# Revit family: IS_Linda-X_T4401_BIM_NL
name_source: partatom
category: Plumbing Fixtures
units: mm (PartAtom-declared; Revit-internal decimal feet)

## family parameters
Always vertical = No
Cut with Voids When Loaded = No
OmniClass Number = 23.45.05.14.14
OmniClass Title = Sinks/Lavatories
Part Type = Normal
Room Calculation Point = No
Round Connector Dimension = Use Diameter
Shared = No
Work Plane-Based = No

## types (13) — shared parameters
Accesoires = https://www.idealstandard.nl
Accessories = https://www.idealstandard.nl
Afmetingen = 380 x 153 x 550mm
AfstandsEenheid = Millimeter
AreaUnits = Millimeter
Artikelomschrijving = Linda-X Gefäßbecken 55cm, ohne Hahnlöcher, geschlitzter Überlauf
Artikelreferentie = Linda-X Vessel Basin 55cm, No Tap Holes, Slotted Overflow
Auteur = Idea Standard
BIMObjectName = IS_IdealStandard_Wallhungwashbasins_Linda-X_T4401
BIMobject category = Sanitary Basins
BIMobject category code = sanitary-basins
BIMobject main category = Sanitary
BIMobject main category code = sanitary
Beschrijvinggarantie = Herstellergarantie
BimObjectNaam = IS_IdealStandard_Wallhungwashbasins_Linda-X_T4401
Brand = Idea Standard
Brand url = http://www.idealstandard.nl
ConnectionType = Plumbing
CurrencyUnit = €
CurrentRevision = 1
Date of publishing = 14/07/2021
Description = Linda-X Gefäßbecken 55cm, ohne Hahnlöcher, geschlitzter Überlauf
DurationUnit = Years
DuurEenheid = Jahre
Edition number = 1
Eigenschappen = Gefäßbecken 55cm, ohne Hahnlöcher, geschlitzter Überlauf
ElementType = Fixed
Features = Gefäßbecken 55cm, ohne Hahnlöcher, geschlitzter Überlauf
Garantieunits = Jahren
Help = https://www.idealstandard.nl
Hoogte = 153.310487747192
Hulp = https://www.idealstandard.nl
IFC Classification = Sanitary Terminal
IfcExportAs = IfcSanitaryTerminalType
IfcExportType = WASHHANDBASIN
Installatieinstructies = https://www.idealstandard.nl
Installation instructions = https://www.idealstandard.nl
InstallationInstructions = https://www.idealstandard.nl
Lengte = 380 mm
LinearUnits = Millimetres
MaintenanceInformation = https://www.idealstandard.nl
Manufacturer = Ideal Standard
Manufacturer name = Ideal Standard
ManufacturerURL = https://www.idealstandard.nl
Masterformat 2014 Code = 33 44 13.13
Masterformat 2014 Description = Catchbasins
Materiaal = Keramik
Material = Diamatec
Material main = Keramik
Merk = Ideal Standard
ModelReference = Linda-X Vessel Basin 55cm, No Tap Holes, Slotted Overflow
Montageinstuctie = https://www.idealstandard.nl
NBS Reference Code = 45-35-70/369
NBS Reference Description = Wall hung wash basins
Name = Wallhungwashbasins_Linda-X_T4401_IdealStandard
NettWeight = 12.4
NominalDepth = 380 mm
NominalHeight = 153 mm
NominalWidth = 550 mm
Normen = Wallhungwashbasins_Linda-X_T4401_IdealStandard
OmniClass Code = 23-39 29 13 21 19
OmniClass Description = Surface Water Retention Basins
Ophangingwastafel = Wand oder Sockel installiert
OppervlakteEenheid = Millimeter
Product Guid = 11f8b192-65c3-4091-a7fc-1ee436633e5b
Product SKU = T4401
Product certification = https://www.idealstandard.nl
Product data url = https://bimobject.com
Product family = Linda-X
Product group = Washbasins
Product name = Linda-X Vessel Basin 55cm, No Tap Holes, Slotted Overflow
Product url = https://www.idealstandard.nl
ProductInformation = https://www.idealstandard.nl
Productinformatie = https://www.idealstandard.nl
QR code = http://bimobject.com
Referentie = Linda-X Vessel Basin 55cm, No Tap Holes, Slotted Overflow
Revisie = 1
Shape = Oval
Size = 380 x 153 x 550mm
Space = Internal
SpareParts = https://www.idealstandard.nl
Technical description = https://www.idealstandard.nl
Telefoonnummer = 077 355 08 08
Typeconnectie = Installation
Typewastafel = Oval, Wand oder Sockel installiert
UNSPSC Code = 301815
URL = https://www.idealstandard.nl
Uniclass 1.4 Code = L7212
Uniclass 1.4 Description = Washbasins
Uniclass 2.0 Code = PR-31-79
Uniclass 2.0 Description = Sinks, Wash Basins And Troughs
Uniclass 2015 Code = Pr_40_20_96_96
Uniclass 2015 Name = Wall-hung washbasins
Uniclass2015Beschrijving = Wall-hung washbasins
Uniclass2015Code = Pr_40_20_96_96
Uniclass2015Referentie = Pr_40_20_96_96
Uniclass2015Title = Wall-hung washbasins
Uniclass2015Version = v1.20
Urlproducent = https://www.idealstandard.nl
ValutaEenheid = €
Versie = 1
Version = 1
VolumeUnits = Litres
Volumeunits = Liter
Vorm = Oval
WRASURL = https://www.wrasapprovals.co.uk
WarrantyDescription = Manufacturer Warranty
WarrantyDurationUnit = 5
WashHandBasinMounting = Wall Hung
WashHandBasinType = Vessel Wash Basin
Wisselstukken = https://www.idealstandard.nl
Youtube clip = https://www.youtube.com
zero-valued in all types: Breedte, BrutoGewicht, Cost, Diepte, MaterialThickness, Nettogewicht, OutletConnectionSize, Vervangingskosten

## per-type parameters (varying)
| type | Afwerking | Artikelnummer | BarCode | Barcode | Color | Finish | GTIN code | Kleur | MainColor | Model | ModelNumber |
| T440101 - Linda-X Vessel Basin 55cm, No Tap Holes, Slotted Overflow - Gloss White | Glänzend weiß | T440101 | 8014140484974 | 8014140484974 | Glänzend weiß | Glänzend weiß | https://8014140484974 | Glänzend weiß | White | T440101 | T440101 |
| T4401MA - Linda-X Vessel Basin 55cm, No Tap Holes, Slotted Overflow - Ideal Plus White | IdealPlusWeiß | T4401MA | 8014140490418 | 8014140490418 | IdealPlusWeiß | IdealPlusWeiß | https://8014140490418 | IdealPlusWeiß | Ideal Plus White | T4401MA | T4401MA |
| T4401V1 - Linda-X Vessel Basin 55cm, No Tap Holes, Slotted Overflow - Silk White | Seidenweiß | T4401V1 | 8014140484981 | 8014140484981 | Seidenweiß | Seidenweiß | https://8014140484981 | Seidenweiß | Silk White | T4401V1 | T4401V1 |
| T4401V2 - Linda-X Vessel Basin 55cm, No Tap Holes, Slotted Overflow - Black Gloss | SchwarzGlanz | T4401V2 |  |  | SchwarzGlanz | SchwarzGlanz |  | SchwarzGlanz | Black Gloss | T4401V2 | T4401V2 |
| T4401V3 - Linda-X Vessel Basin 55cm, No Tap Holes, Slotted Overflow - Silk Black | SeideSchwarz | T4401V3 |  |  | SeideSchwarz | SeideSchwarz |  | SeideSchwarz | Silk Black | T4401V3 | T4401V3 |
| T4401V4 - Linda-X Vessel Basin 55cm, No Tap Holes, Slotted Overflow - Kashmir | Kaschmir | T4401V4 |  |  | Kaschmir | Kaschmir |  | Kaschmir | Kashmir | T4401V4 | T4401V4 |
| T4401V5 - Linda-X Vessel Basin 55cm, No Tap Holes, Slotted Overflow - Slate Grey | Schiefergrau | T4401V5 |  |  | Schiefergrau | Schiefergrau |  | Schiefergrau | Slate Grey | T4401V5 | T4401V5 |
| T4401V6 - Linda-X Vessel Basin 55cm, No Tap Holes, Slotted Overflow - Pomegranate | Granatapfel | T4401V6 |  |  | Granatapfel | Granatapfel |  | Granatapfel | Pomegranate | T4401V6 | T4401V6 |
| T4401V7 - Linda-X Vessel Basin 55cm, No Tap Holes, Slotted Overflow - Nude | Nackt | T4401V7 |  |  | Nackt | Nackt |  | Nackt | Nude | T4401V7 | T4401V7 |
| T4401V8 - Linda-X Vessel Basin 55cm, No Tap Holes, Slotted Overflow - Mink | Nerz | T4401V8 |  |  | Nerz | Nerz |  | Nerz | Mink | T4401V8 | T4401V8 |
| T4401V9 - Linda-X Vessel Basin 55cm, No Tap Holes, Slotted Overflow - Concrete | Beton | T4401V9 |  |  | Beton | Beton |  | Beton | Concrete | T4401V9 | T4401V9 |
| T4401X8 - Linda-X Vessel Basin 55cm, No Tap Holes, Slotted Overflow - Powder | Pulver | T4401X8 |  |  | Pulver | Pulver |  | Pulver | Powder | T4401X8 | T4401X8 |
| T4401X9 - Linda-X Vessel Basin 55cm, No Tap Holes, Slotted Overflow - Sage | Salbei | T4401X9 |  |  | Salbei | Salbei |  | Salbei | Sage | T4401X9 | T4401X9 |

## geometry (parser evidence)
native form markers: Sweep x1
no freeform markers — native parametric forms only
